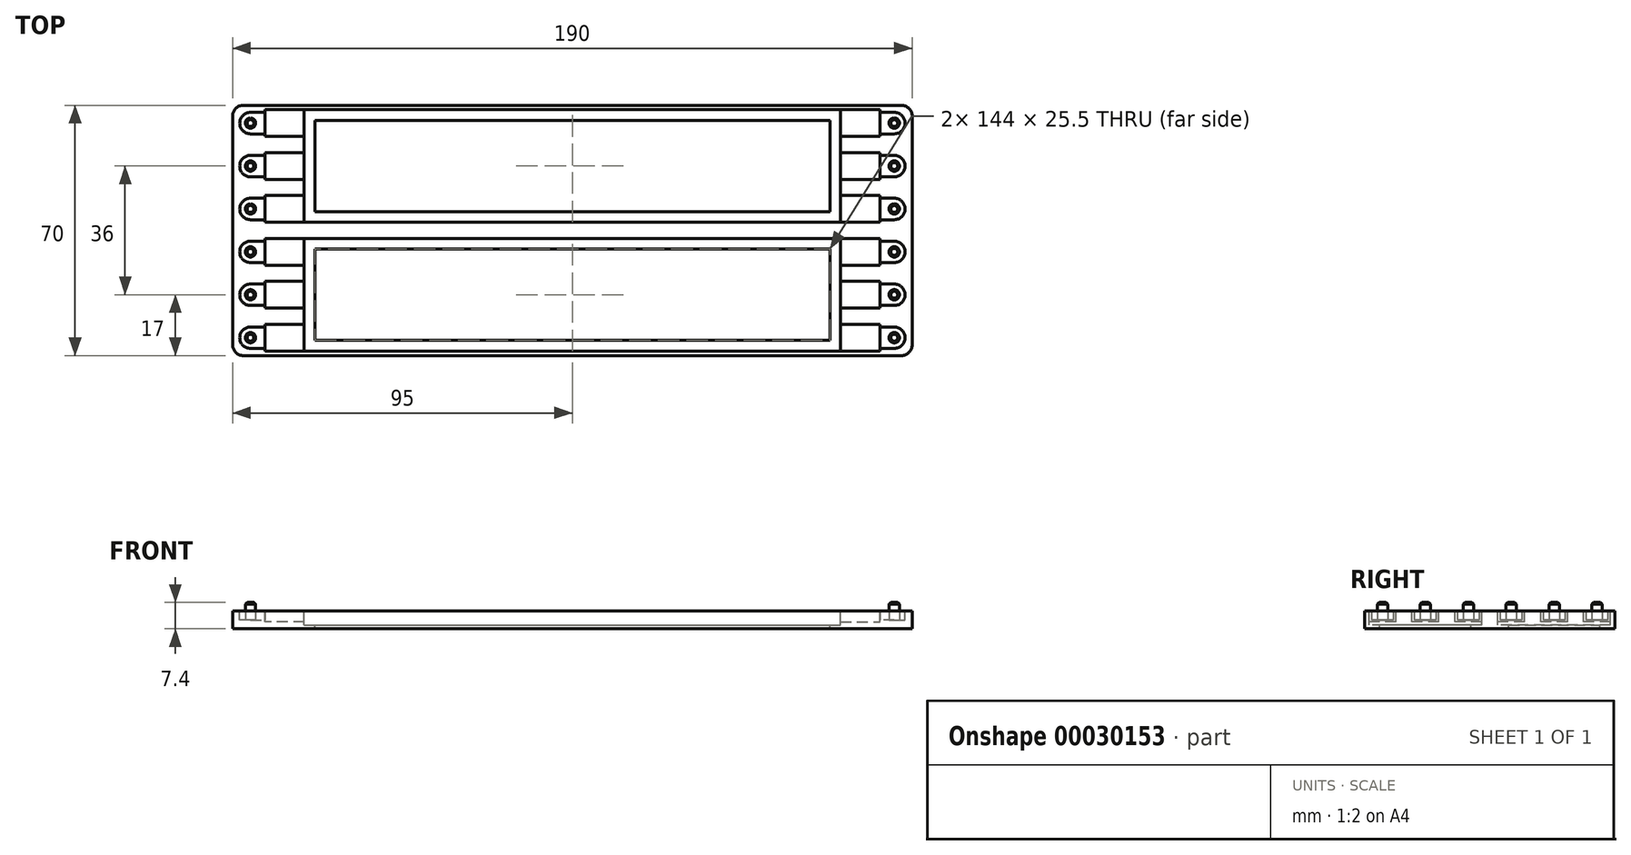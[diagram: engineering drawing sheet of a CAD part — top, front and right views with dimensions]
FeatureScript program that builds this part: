
annotation { "Feature Type Name" : "Feature", "Feature Type Description" : "" }
export const myFeature = defineFeature(function(context is Context, id is Id, definition is map)
    precondition{}
    {
        {
            var Q0;
            Q0=qCreatedBy(makeId("Top.planeOp"),FACE);
            var sketch = newSketch(context, id + "F0", { "sketchPlane" : qUnion([Q0])});
            skLineSegment(sketch, "E0.rect.bottom", {"start": v(-5, 65) * mm, "end": v(15, 65) * mm});
            skLineSegment(sketch, "E0.rect.top", {"start": v(-5, -5) * mm, "end": v(15, -5) * mm});
            skLineSegment(sketch, "E0.rect.left", {"start": v(-5, 65) * mm, "end": v(-5, -5) * mm});
            skLineSegment(sketch, "E0.rect.right", {"start": v(15, 65) * mm, "end": v(15, -5) * mm});
            skCircle(sketch, "E1", {"center": v(0, 0) * mm, "radius": 5 * mm, "construction": true});
            skSolve(sketch);
        }
        {
            var Q0;
            Q0=makeQuery(id+"F0.imprint","IMPRINT",FACE,{"disambiguationData":[TD([[makeQuery(id+"F0.imprint","IMPRINT",EDGE,{"derivedFrom":sQuery(id+"F0.wireOp",EDGE,"E0.rect.bottom")}),-1.0]])]});
            extrude(context, id + "F1", {"entities" : qUnion([Q0]), "depth" : 4 * mm});
        }
        {
            var Q0;
            Q0=makeQuery(id+"F1.opExtrude","CAP_FACE",FACE,{"disambiguationData":[OSD([sQuery(id+"F0.wireOp",EDGE,"E0.rect.bottom"),sQuery(id+"F0.wireOp",EDGE,"E0.rect.top"),sQuery(id+"F0.wireOp",EDGE,"E0.rect.left"),sQuery(id+"F0.wireOp",EDGE,"E0.rect.right")])],"isStart":false});
            var sketch = newSketch(context, id + "F2", { "sketchPlane" : qUnion([Q0])});
            skArc(sketch, "E2", {"start": v(0, 3) * mm, "mid": v(-3, 0) * mm, "end": v(0, -3) * mm});
            skLineSegment(sketch, "E3", {"start": v(0, 3) * mm, "end": v(15, 3) * mm});
            skLineSegment(sketch, "E4", {"start": v(15, 3) * mm, "end": v(15, -3) * mm});
            skLineSegment(sketch, "E5", {"start": v(15, -3) * mm, "end": v(0, -3) * mm});
            skPoint(sketch, "E6", {"position": v(15, 0) * mm});
            skPoint(sketch, "E7.0.1.0", {"position": v(15, 12) * mm});
            skArc(sketch, "E7.0.1.1", {"start": v(0, 15) * mm, "mid": v(-3, 12) * mm, "end": v(0, 9) * mm});
            skLineSegment(sketch, "E7.0.1.2", {"start": v(0, 15) * mm, "end": v(15, 15) * mm});
            skLineSegment(sketch, "E7.0.1.3", {"start": v(15, 15) * mm, "end": v(15, 9) * mm});
            skLineSegment(sketch, "E7.0.1.4", {"start": v(15, 9) * mm, "end": v(0, 9) * mm});
            skPoint(sketch, "E7.0.2.0", {"position": v(15, 24) * mm});
            skArc(sketch, "E7.0.2.1", {"start": v(0, 27) * mm, "mid": v(-3, 24) * mm, "end": v(0, 21) * mm});
            skLineSegment(sketch, "E7.0.2.2", {"start": v(0, 27) * mm, "end": v(15, 27) * mm});
            skLineSegment(sketch, "E7.0.2.3", {"start": v(15, 27) * mm, "end": v(15, 21) * mm});
            skLineSegment(sketch, "E7.0.2.4", {"start": v(15, 21) * mm, "end": v(0, 21) * mm});
            skPoint(sketch, "E7.0.3.0", {"position": v(15, 36) * mm});
            skArc(sketch, "E7.0.3.1", {"start": v(0, 39) * mm, "mid": v(-3, 36) * mm, "end": v(0, 33) * mm});
            skLineSegment(sketch, "E7.0.3.2", {"start": v(0, 39) * mm, "end": v(15, 39) * mm});
            skLineSegment(sketch, "E7.0.3.3", {"start": v(15, 39) * mm, "end": v(15, 33) * mm});
            skLineSegment(sketch, "E7.0.3.4", {"start": v(15, 33) * mm, "end": v(0, 33) * mm});
            skPoint(sketch, "E7.0.4.0", {"position": v(15, 48) * mm});
            skArc(sketch, "E7.0.4.1", {"start": v(0, 51) * mm, "mid": v(-3, 48) * mm, "end": v(0, 45) * mm});
            skLineSegment(sketch, "E7.0.4.2", {"start": v(0, 51) * mm, "end": v(15, 51) * mm});
            skLineSegment(sketch, "E7.0.4.3", {"start": v(15, 51) * mm, "end": v(15, 45) * mm});
            skLineSegment(sketch, "E7.0.4.4", {"start": v(15, 45) * mm, "end": v(0, 45) * mm});
            skPoint(sketch, "E7.0.5.0", {"position": v(15, 60) * mm});
            skArc(sketch, "E7.0.5.1", {"start": v(0, 63) * mm, "mid": v(-3, 60) * mm, "end": v(0, 57) * mm});
            skLineSegment(sketch, "E7.0.5.2", {"start": v(0, 63) * mm, "end": v(15, 63) * mm});
            skLineSegment(sketch, "E7.0.5.3", {"start": v(15, 63) * mm, "end": v(15, 57) * mm});
            skLineSegment(sketch, "E7.0.5.4", {"start": v(15, 57) * mm, "end": v(0, 57) * mm});
            skLineSegment(sketch, "E7.direction1", {"start": v(15, 0) * mm, "end": v(40, 0) * mm, "construction": true});
            skLineSegment(sketch, "E7.direction2", {"start": v(15, 0) * mm, "end": v(15, 12) * mm, "construction": true});
            skLineSegment(sketch, "E8", {"start": v(0, 3) * mm, "end": v(0, -3) * mm, "construction": true});
            skSolve(sketch);
        }
        {
            var Q0;
            Q0 = qSketchRegion(id + "F2", true);
            extrude(context, id + "F3", {"entities" : qUnion([Q0]), "operationType" : NewBodyOperationType.REMOVE, "oppositeDirection" : true, "depth" : 2.6 * mm});
        }
        {
            var Q0;
            Q0=makeQuery(id+"F1.opExtrude","CAP_FACE",FACE,{"disambiguationData":[OSD([sQuery(id+"F0.wireOp",EDGE,"E0.rect.bottom"),sQuery(id+"F0.wireOp",EDGE,"E0.rect.top"),sQuery(id+"F0.wireOp",EDGE,"E0.rect.left"),sQuery(id+"F0.wireOp",EDGE,"E0.rect.right")])],"isStart":false});
            var sketch = newSketch(context, id + "F4", { "sketchPlane" : qUnion([Q0])});
            skLineSegment(sketch, "E9.top", {"start": v(15, 3.75) * mm, "end": v(4, 3.75) * mm});
            skLineSegment(sketch, "E10.top", {"start": v(15, -3.75) * mm, "end": v(4, -3.75) * mm});
            skLineSegment(sketch, "E10.right", {"start": v(4, 3.75) * mm, "end": v(4, -3.75) * mm});
            skCircle(sketch, "E11", {"center": v(0, 0) * mm, "radius": 3 * mm, "construction": true});
            skPoint(sketch, "E11.first.point", {"position": v(-1.02, 2.82) * mm});
            skPoint(sketch, "E11.second.point", {"position": v(-2.95, 0.56) * mm});
            skPoint(sketch, "E11.third.point", {"position": v(-1.82, -2.38) * mm});
            skCircle(sketch, "E12.0.1.0", {"center": v(0, 12) * mm, "radius": 3 * mm, "construction": true});
            skPoint(sketch, "E12.0.1.2", {"position": v(-1.82, 9.62) * mm});
            skPoint(sketch, "E12.0.1.3", {"position": v(-1.02, 14.82) * mm});
            skLineSegment(sketch, "E12.0.1.5", {"start": v(15, 15.75) * mm, "end": v(4, 15.75) * mm});
            skLineSegment(sketch, "E12.0.1.6", {"start": v(15, 8.25) * mm, "end": v(4, 8.25) * mm});
            skPoint(sketch, "E12.0.1.7", {"position": v(-2.95, 12.56) * mm});
            skLineSegment(sketch, "E12.0.1.8", {"start": v(4, 15.75) * mm, "end": v(4, 8.25) * mm});
            skLineSegment(sketch, "E12.0.1.9", {"start": v(4, 15) * mm, "end": v(4, 15.75) * mm});
            skLineSegment(sketch, "E12.0.1.10", {"start": v(15, 15) * mm, "end": v(15, 15.75) * mm});
            skLineSegment(sketch, "E12.0.1.11", {"start": v(15, 9) * mm, "end": v(15, 8.25) * mm});
            skCircle(sketch, "E12.0.2.0", {"center": v(0, 24) * mm, "radius": 3 * mm, "construction": true});
            skPoint(sketch, "E12.0.2.2", {"position": v(-1.82, 21.62) * mm});
            skPoint(sketch, "E12.0.2.3", {"position": v(-1.02, 26.82) * mm});
            skLineSegment(sketch, "E12.0.2.5", {"start": v(15, 27.75) * mm, "end": v(4, 27.75) * mm});
            skLineSegment(sketch, "E12.0.2.6", {"start": v(15, 20.25) * mm, "end": v(4, 20.25) * mm});
            skPoint(sketch, "E12.0.2.7", {"position": v(-2.95, 24.56) * mm});
            skLineSegment(sketch, "E12.0.2.8", {"start": v(4, 27.75) * mm, "end": v(4, 20.25) * mm});
            skLineSegment(sketch, "E12.0.2.9", {"start": v(4, 27) * mm, "end": v(4, 27.75) * mm});
            skLineSegment(sketch, "E12.0.2.10", {"start": v(15, 27) * mm, "end": v(15, 27.75) * mm});
            skLineSegment(sketch, "E12.0.2.11", {"start": v(15, 21) * mm, "end": v(15, 20.25) * mm});
            skCircle(sketch, "E12.0.3.0", {"center": v(0, 36) * mm, "radius": 3 * mm, "construction": true});
            skPoint(sketch, "E12.0.3.2", {"position": v(-1.82, 33.62) * mm});
            skPoint(sketch, "E12.0.3.3", {"position": v(-1.02, 38.82) * mm});
            skLineSegment(sketch, "E12.0.3.5", {"start": v(15, 39.75) * mm, "end": v(4, 39.75) * mm});
            skLineSegment(sketch, "E12.0.3.6", {"start": v(15, 32.25) * mm, "end": v(4, 32.25) * mm});
            skPoint(sketch, "E12.0.3.7", {"position": v(-2.95, 36.56) * mm});
            skLineSegment(sketch, "E12.0.3.8", {"start": v(4, 39.75) * mm, "end": v(4, 32.25) * mm});
            skLineSegment(sketch, "E12.0.3.9", {"start": v(4, 39) * mm, "end": v(4, 39.75) * mm});
            skLineSegment(sketch, "E12.0.3.10", {"start": v(15, 39) * mm, "end": v(15, 39.75) * mm});
            skLineSegment(sketch, "E12.0.3.11", {"start": v(15, 33) * mm, "end": v(15, 32.25) * mm});
            skCircle(sketch, "E12.0.4.0", {"center": v(0, 48) * mm, "radius": 3 * mm, "construction": true});
            skPoint(sketch, "E12.0.4.2", {"position": v(-1.82, 45.62) * mm});
            skPoint(sketch, "E12.0.4.3", {"position": v(-1.02, 50.82) * mm});
            skLineSegment(sketch, "E12.0.4.5", {"start": v(15, 51.75) * mm, "end": v(4, 51.75) * mm});
            skLineSegment(sketch, "E12.0.4.6", {"start": v(15, 44.25) * mm, "end": v(4, 44.25) * mm});
            skPoint(sketch, "E12.0.4.7", {"position": v(-2.95, 48.56) * mm});
            skLineSegment(sketch, "E12.0.4.8", {"start": v(4, 51.75) * mm, "end": v(4, 44.25) * mm});
            skLineSegment(sketch, "E12.0.4.9", {"start": v(4, 51) * mm, "end": v(4, 51.75) * mm});
            skLineSegment(sketch, "E12.0.4.10", {"start": v(15, 51) * mm, "end": v(15, 51.75) * mm});
            skLineSegment(sketch, "E12.0.4.11", {"start": v(15, 45) * mm, "end": v(15, 44.25) * mm});
            skCircle(sketch, "E12.0.5.0", {"center": v(0, 60) * mm, "radius": 3 * mm, "construction": true});
            skPoint(sketch, "E12.0.5.2", {"position": v(-1.82, 57.62) * mm});
            skPoint(sketch, "E12.0.5.3", {"position": v(-1.02, 62.82) * mm});
            skLineSegment(sketch, "E12.0.5.5", {"start": v(15, 63.75) * mm, "end": v(4, 63.75) * mm});
            skLineSegment(sketch, "E12.0.5.6", {"start": v(15, 56.25) * mm, "end": v(4, 56.25) * mm});
            skPoint(sketch, "E12.0.5.7", {"position": v(-2.95, 60.56) * mm});
            skLineSegment(sketch, "E12.0.5.8", {"start": v(4, 63.75) * mm, "end": v(4, 56.25) * mm});
            skLineSegment(sketch, "E12.0.5.9", {"start": v(4, 63) * mm, "end": v(4, 63.75) * mm});
            skLineSegment(sketch, "E12.0.5.10", {"start": v(15, 63) * mm, "end": v(15, 63.75) * mm});
            skLineSegment(sketch, "E12.0.5.11", {"start": v(15, 57) * mm, "end": v(15, 56.25) * mm});
            skLineSegment(sketch, "E12.direction1", {"start": v(0, 0) * mm, "end": v(25, 0) * mm, "construction": true});
            skLineSegment(sketch, "E12.direction2", {"start": v(0, 0) * mm, "end": v(0, 12) * mm, "construction": true});
            skLineSegment(sketch, "E13", {"start": v(15, 3.75) * mm, "end": v(15, -3.75) * mm});
            skPoint(sketch, "E14", {"position": v(15, 0) * mm});
            skLineSegment(sketch, "E15", {"start": v(15, 21) * mm, "end": v(15, 27) * mm});
            skLineSegment(sketch, "E16", {"start": v(15, 33) * mm, "end": v(15, 39) * mm});
            skLineSegment(sketch, "E17", {"start": v(15, 63) * mm, "end": v(15, 57) * mm});
            skLineSegment(sketch, "E18", {"start": v(15, 51) * mm, "end": v(15, 45) * mm});
            skLineSegment(sketch, "E19", {"start": v(15, 15) * mm, "end": v(15, 9) * mm});
            skSolve(sketch);
        }
        {
            var Q0;
            Q0 = qSketchRegion(id + "F4", true);
            var Q1;
            Q1=makeQuery(id+"F3.boolean.opBoolean","COPY",FACE,{"derivedFrom":makeQuery(id+"F3.opExtrude","CAP_FACE",FACE,{"disambiguationData":[OSD([sQuery(id+"F2.wireOp",EDGE,"E2"),sQuery(id+"F2.wireOp",EDGE,"E3"),sQuery(id+"F2.wireOp",EDGE,"E4"),sQuery(id+"F2.wireOp",EDGE,"E5")])],"isStart":false})});
            extrude(context, id + "F5", {"entities" : qUnion([Q0]), "operationType" : NewBodyOperationType.REMOVE, "oppositeDirection" : true, "endBoundEntityFace" : qUnion([Q1]), "depth" : 3 * mm});
        }
        {
            var Q0;
            Q0=makeQuery(id+"F3.boolean.opBoolean","COPY",FACE,{"derivedFrom":makeQuery(id+"F3.opExtrude","CAP_FACE",FACE,{"disambiguationData":[OSD([sQuery(id+"F2.wireOp",EDGE,"E2")])],"isStart":false})});
            var sketch = newSketch(context, id + "F6", { "sketchPlane" : qUnion([Q0])});
            skCircle(sketch, "E20", {"center": v(0, 0) * mm, "radius": 1.45 * mm});
            skCircle(sketch, "E21.0.1.0", {"center": v(0, 12) * mm, "radius": 1.45 * mm});
            skCircle(sketch, "E21.0.2.0", {"center": v(0, 24) * mm, "radius": 1.45 * mm});
            skCircle(sketch, "E21.0.3.0", {"center": v(0, 36) * mm, "radius": 1.45 * mm});
            skCircle(sketch, "E21.0.4.0", {"center": v(0, 48) * mm, "radius": 1.45 * mm});
            skCircle(sketch, "E21.0.5.0", {"center": v(0, 60) * mm, "radius": 1.45 * mm});
            skLineSegment(sketch, "E21.direction1", {"start": v(0, 0) * mm, "end": v(25, 0) * mm, "construction": true});
            skLineSegment(sketch, "E21.direction2", {"start": v(0, 0) * mm, "end": v(0, 12) * mm, "construction": true});
            skSolve(sketch);
        }
        {
            var Q0;
            Q0=makeQuery(id+"F6.imprint","IMPRINT",FACE,{"disambiguationData":[TD([[makeQuery(id+"F6.imprint","IMPRINT",EDGE,{"derivedFrom":sQuery(id+"F6.wireOp",EDGE,"E20")}),1.0]])]});
            var Q1;
            Q1=makeQuery(id+"F6.imprint","IMPRINT",FACE,{"disambiguationData":[TD([[makeQuery(id+"F6.imprint","IMPRINT",EDGE,{"derivedFrom":sQuery(id+"F6.wireOp",EDGE,"E21.0.1.0")}),1.0]])]});
            var Q2;
            Q2=makeQuery(id+"F6.imprint","IMPRINT",FACE,{"disambiguationData":[TD([[makeQuery(id+"F6.imprint","IMPRINT",EDGE,{"derivedFrom":sQuery(id+"F6.wireOp",EDGE,"E21.0.2.0")}),1.0]])]});
            var Q3;
            Q3=makeQuery(id+"F6.imprint","IMPRINT",FACE,{"disambiguationData":[TD([[makeQuery(id+"F6.imprint","IMPRINT",EDGE,{"derivedFrom":sQuery(id+"F6.wireOp",EDGE,"E21.0.3.0")}),1.0]])]});
            var Q4;
            Q4=makeQuery(id+"F6.imprint","IMPRINT",FACE,{"disambiguationData":[TD([[makeQuery(id+"F6.imprint","IMPRINT",EDGE,{"derivedFrom":sQuery(id+"F6.wireOp",EDGE,"E21.0.4.0")}),1.0]])]});
            var Q5;
            Q5=makeQuery(id+"F6.imprint","IMPRINT",FACE,{"disambiguationData":[TD([[makeQuery(id+"F6.imprint","IMPRINT",EDGE,{"derivedFrom":sQuery(id+"F6.wireOp",EDGE,"E21.0.5.0")}),1.0]])]});
            extrude(context, id + "F7", {"entities" : qUnion([Q0, Q1, Q2, Q3, Q4, Q5]), "operationType" : NewBodyOperationType.ADD, "depth" : 5 * mm});
        }
        {
            var Q0;
            Q0=makeQuery(id+"F7.opExtrude","CAP_EDGE",EDGE,{"disambiguationData":[OSD([sQuery(id+"F6.wireOp",EDGE,"E20")])],"isStart":false});
            var Q1;
            Q1=makeQuery(id+"F7.opExtrude","CAP_EDGE",EDGE,{"disambiguationData":[OSD([sQuery(id+"F6.wireOp",EDGE,"E21.0.1.0")])],"isStart":false});
            var Q2;
            Q2=makeQuery(id+"F7.opExtrude","CAP_EDGE",EDGE,{"disambiguationData":[OSD([sQuery(id+"F6.wireOp",EDGE,"E21.0.2.0")])],"isStart":false});
            var Q3;
            Q3=makeQuery(id+"F7.opExtrude","CAP_EDGE",EDGE,{"disambiguationData":[OSD([sQuery(id+"F6.wireOp",EDGE,"E21.0.3.0")])],"isStart":false});
            var Q4;
            Q4=makeQuery(id+"F7.opExtrude","CAP_EDGE",EDGE,{"disambiguationData":[OSD([sQuery(id+"F6.wireOp",EDGE,"E21.0.5.0")])],"isStart":false});
            var Q5;
            Q5=makeQuery(id+"F7.opExtrude","CAP_EDGE",EDGE,{"disambiguationData":[OSD([sQuery(id+"F6.wireOp",EDGE,"E21.0.4.0")])],"isStart":false});
            chamfer(context, id + "F8", {"entities" : qUnion([Q0, Q1, Q2, Q3, Q4, Q5]), "width" : .5 * mm, "tangentPropagation" : true});
        }
        {
            var Q0;
            Q0=makeQuery(id+"F1.opExtrude","CAP_FACE",FACE,{"disambiguationData":[OSD([sQuery(id+"F0.wireOp",EDGE,"E0.rect.bottom"),sQuery(id+"F0.wireOp",EDGE,"E0.rect.top"),sQuery(id+"F0.wireOp",EDGE,"E0.rect.left"),sQuery(id+"F0.wireOp",EDGE,"E0.rect.right")])],"isStart":true});
            var sketch = newSketch(context, id + "F9", { "sketchPlane" : qUnion([Q0])});
            skSolve(sketch);
        }
        {
            var Q0;
            Q0=makeQuery(id+"F9.imprint","IMPRINT",FACE,{"disambiguationData":[TD([[makeQuery(id+"F9.imprint","IMPRINT",EDGE,{"derivedFrom":makeQuery(id+"F1.opExtrude","CAP_EDGE",EDGE,{"disambiguationData":[OSD([sQuery(id+"F0.wireOp",EDGE,"E0.rect.bottom")])],"isStart":true})}),1.0]])]});
            var sketch = newSketch(context, id + "F10", { "sketchPlane" : qUnion([Q0])});
            skLineSegment(sketch, "E22.bottom", {"start": v(-5, 5) * mm, "end": v(90, 5) * mm});
            skLineSegment(sketch, "E22.top", {"start": v(-5, -65) * mm, "end": v(90, -65) * mm});
            skLineSegment(sketch, "E22.left", {"start": v(-5, 5) * mm, "end": v(-5, -65) * mm});
            skLineSegment(sketch, "E22.right", {"start": v(90, 5) * mm, "end": v(90, -65) * mm});
            skSolve(sketch);
        }
        {
            var Q0;
            {var subQ2=sQuery(id+"F10.wireOp",EDGE,"E22.right");Q0=makeQuery(id+"F10.imprint","IMPRINT",FACE,{"disambiguationData":[TD([[makeQuery(id+"F10.imprint","IMPRINT",EDGE,{"derivedFrom":subQ2}),-1.0]])]});}
            var Q1;
            Q1=makeQuery(id+"F9.imprint","IMPRINT",FACE,{"disambiguationData":[TD([[makeQuery(id+"F9.imprint","IMPRINT",EDGE,{"derivedFrom":makeQuery(id+"F1.opExtrude","CAP_EDGE",EDGE,{"disambiguationData":[OSD([sQuery(id+"F0.wireOp",EDGE,"E0.rect.bottom")])],"isStart":true})}),1.0]])]});
            extrude(context, id + "F11", {"entities" : qUnion([Q0, Q1]), "operationType" : NewBodyOperationType.ADD, "depth" : 1 * mm});
        }
        {
            var Q0;
            Q0=makeQuery(id+"F11.opExtrude","SWEPT_FACE",FACE,{"disambiguationData":[OSD([sQuery(id+"F10.wireOp",EDGE,"E22.right")])]});
            cPlane(context, id + "F12", {"entities" : qUnion([Q0]), "cplaneType" : CPlaneType.OFFSET, "offset" : 0 * mm, "width" : 150 * mm, "height" : 150 * mm});
        }
        {
            var Q0;
            Q0=makeQuery(id+"F1.opExtrude","SWEPT_BODY",BODY,{"disambiguationData":[OSD([sQuery(id+"F0.wireOp",EDGE,"E0.rect.bottom"),sQuery(id+"F0.wireOp",EDGE,"E0.rect.top"),sQuery(id+"F0.wireOp",EDGE,"E0.rect.left"),sQuery(id+"F0.wireOp",EDGE,"E0.rect.right")])]});
            var Q1;
            Q1=qCreatedBy(id+"F12.planeOp",FACE);
            mirror(context, id + "F13", {"operationType" : NewBodyOperationType.ADD, "entities" : qUnion([Q0]), "mirrorPlane" : qUnion([Q1])});
        }
        {
            var Q0;
            Q0=makeQuery(id+"F1.opExtrude","CAP_FACE",FACE,{"disambiguationData":[OSD([sQuery(id+"F0.wireOp",EDGE,"E0.rect.bottom"),sQuery(id+"F0.wireOp",EDGE,"E0.rect.top"),sQuery(id+"F0.wireOp",EDGE,"E0.rect.left"),sQuery(id+"F0.wireOp",EDGE,"E0.rect.right")])],"isStart":false});
            var sketch = newSketch(context, id + "F14", { "sketchPlane" : qUnion([Q0])});
            skLineSegment(sketch, "E23.bottom", {"start": v(15, -5) * mm, "end": v(165, -5) * mm});
            skLineSegment(sketch, "E23.top", {"start": v(15, -3.75) * mm, "end": v(165, -3.75) * mm});
            skLineSegment(sketch, "E23.left", {"start": v(15, -5) * mm, "end": v(15, -3.75) * mm});
            skLineSegment(sketch, "E23.right", {"start": v(165, -5) * mm, "end": v(165, -3.75) * mm});
            skLineSegment(sketch, "E24.bottom", {"start": v(15, 27.75) * mm, "end": v(165, 27.75) * mm});
            skLineSegment(sketch, "E24.top", {"start": v(15, 32.25) * mm, "end": v(165, 32.25) * mm});
            skLineSegment(sketch, "E24.left", {"start": v(15, 27.75) * mm, "end": v(15, 32.25) * mm});
            skLineSegment(sketch, "E24.right", {"start": v(165, 27.75) * mm, "end": v(165, 32.25) * mm});
            skLineSegment(sketch, "E25.bottom", {"start": v(15, 65) * mm, "end": v(165, 65) * mm});
            skLineSegment(sketch, "E25.top", {"start": v(15, 63.75) * mm, "end": v(165, 63.75) * mm});
            skLineSegment(sketch, "E25.left", {"start": v(15, 65) * mm, "end": v(15, 63.75) * mm});
            skLineSegment(sketch, "E25.right", {"start": v(165, 65) * mm, "end": v(165, 63.75) * mm});
            skSolve(sketch);
        }
        {
            var Q0;
            Q0 = qSketchRegion(id + "F14", true);
            extrude(context, id + "F15", {"entities" : qUnion([Q0]), "operationType" : NewBodyOperationType.ADD, "endBound" : BoundingType.UP_TO_NEXT, "oppositeDirection" : true, "depth" : 25 * mm});
        }
        {
            var Q0;
            {var subQ0=makeQuery(id+"F5.boolean.opBoolean","COPY",FACE,{"derivedFrom":makeQuery(id+"F5.opExtrude","SWEPT_FACE",FACE,{"disambiguationData":[OSD([sQuery(id+"F4.wireOp",EDGE,"E10.top")])]})});var subQ2=sQuery(id+"F0.wireOp",EDGE,"E0.rect.right");var subQ4=makeQuery(id+"F11.boolean.opBoolean","MERGE",FACE,{"derivedFrom":[makeQuery(id+"F11.opExtrude","CAP_FACE",FACE,{"disambiguationData":[OSD([sQuery(id+"F0.wireOp",EDGE,"E0.rect.bottom"),sQuery(id+"F0.wireOp",EDGE,"E0.rect.top"),sQuery(id+"F0.wireOp",EDGE,"E0.rect.left"),subQ2])],"isStart":true}),makeQuery(id+"F11.opExtrude","CAP_FACE",FACE,{"disambiguationData":[OSD([subQ2,sQuery(id+"F10.wireOp",EDGE,"E22.bottom"),sQuery(id+"F10.wireOp",EDGE,"E22.top"),sQuery(id+"F10.wireOp",EDGE,"E22.right")])],"isStart":true})]});Q0=makeQuery(id+"F15.boolean.opBoolean","SPLIT",FACE,{"disambiguationData":[TD([subQ0])],"derivedFrom":makeQuery(id+"F13.boolean.opBoolean","MERGE",FACE,{"derivedFrom":[subQ4,makeQuery(id+"F13.opPattern","COPY",FACE,{"derivedFrom":subQ4,"instanceName":"1"})]})});}
            var sketch = newSketch(context, id + "F16", { "sketchPlane" : qUnion([Q0])});
            skLineSegment(sketch, "E26.bottom", {"start": v(15, 27.75) * mm, "end": v(165, 27.75) * mm, "construction": true});
            skLineSegment(sketch, "E26.top", {"start": v(15, -3.75) * mm, "end": v(165, -3.75) * mm, "construction": true});
            skLineSegment(sketch, "E26.left", {"start": v(15, 27.75) * mm, "end": v(15, -3.75) * mm, "construction": true});
            skLineSegment(sketch, "E26.right", {"start": v(165, 27.75) * mm, "end": v(165, -3.75) * mm, "construction": true});
            skLineSegment(sketch, "E27.0", {"start": v(18, -0.75) * mm, "end": v(162, -0.75) * mm});
            skLineSegment(sketch, "E27.1", {"start": v(18, 24.75) * mm, "end": v(18, -0.75) * mm});
            skLineSegment(sketch, "E27.2", {"start": v(18, 24.75) * mm, "end": v(162, 24.75) * mm});
            skLineSegment(sketch, "E27.3", {"start": v(162, 24.75) * mm, "end": v(162, -0.75) * mm});
            skLineSegment(sketch, "E28", {"start": v(15, 27.75) * mm, "end": v(15, 32.25) * mm, "construction": true});
            skPoint(sketch, "E29", {"position": v(15, 30) * mm});
            skLineSegment(sketch, "E30", {"start": v(165, 27.75) * mm, "end": v(165, 32.25) * mm, "construction": true});
            skPoint(sketch, "E31", {"position": v(165, 30) * mm});
            skLineSegment(sketch, "E32", {"start": v(165, 30) * mm, "end": v(15, 30) * mm, "construction": true});
            skLineSegment(sketch, "E33.MirrorCS", {"start": v(18, 35.25) * mm, "end": v(18, 60.75) * mm});
            skLineSegment(sketch, "E34.MirrorCS", {"start": v(18, 60.75) * mm, "end": v(162, 60.75) * mm});
            skLineSegment(sketch, "E35.MirrorCS", {"start": v(162, 35.25) * mm, "end": v(162, 60.75) * mm});
            skLineSegment(sketch, "E36.MirrorCS", {"start": v(18, 35.25) * mm, "end": v(162, 35.25) * mm});
            skSolve(sketch);
        }
        {
            var Q0;
            Q0 = qSketchRegion(id + "F16", true);
            extrude(context, id + "F17", {"entities" : qUnion([Q0]), "operationType" : NewBodyOperationType.REMOVE, "endBound" : BoundingType.UP_TO_NEXT, "oppositeDirection" : true, "depth" : 25 * mm});
        }
        {
            var Q0;
            {var subQ0=sQuery(id+"F0.wireOp",EDGE,"E0.rect.top");var subQ1=sQuery(id+"F0.wireOp",EDGE,"E0.rect.left");Q0=makeQuery(id+"F11.boolean.opBoolean","MERGE",EDGE,{"derivedFrom":[makeQuery(id+"F1.opExtrude","SWEPT_EDGE",EDGE,{"disambiguationData":[OSD([subQ0,subQ1])]}),makeQuery(id+"F11.opExtrude","SWEPT_EDGE",EDGE,{"disambiguationData":[OSD([subQ0,subQ1])]})]});}
            var Q1;
            {var subQ0=sQuery(id+"F0.wireOp",EDGE,"E0.rect.top");var subQ1=sQuery(id+"F0.wireOp",EDGE,"E0.rect.left");Q1=makeQuery(id+"F13.opPattern","COPY",EDGE,{"derivedFrom":makeQuery(id+"F11.boolean.opBoolean","MERGE",EDGE,{"derivedFrom":[makeQuery(id+"F1.opExtrude","SWEPT_EDGE",EDGE,{"disambiguationData":[OSD([subQ0,subQ1])]}),makeQuery(id+"F11.opExtrude","SWEPT_EDGE",EDGE,{"disambiguationData":[OSD([subQ0,subQ1])]})]}),"instanceName":"1"});}
            var Q2;
            {var subQ0=sQuery(id+"F0.wireOp",EDGE,"E0.rect.bottom");var subQ1=sQuery(id+"F0.wireOp",EDGE,"E0.rect.left");Q2=makeQuery(id+"F13.opPattern","COPY",EDGE,{"derivedFrom":makeQuery(id+"F11.boolean.opBoolean","MERGE",EDGE,{"derivedFrom":[makeQuery(id+"F1.opExtrude","SWEPT_EDGE",EDGE,{"disambiguationData":[OSD([subQ0,subQ1])]}),makeQuery(id+"F11.opExtrude","SWEPT_EDGE",EDGE,{"disambiguationData":[OSD([subQ0,subQ1])]})]}),"instanceName":"1"});}
            var Q3;
            {var subQ0=sQuery(id+"F0.wireOp",EDGE,"E0.rect.bottom");var subQ1=sQuery(id+"F0.wireOp",EDGE,"E0.rect.left");Q3=makeQuery(id+"F11.boolean.opBoolean","MERGE",EDGE,{"derivedFrom":[makeQuery(id+"F1.opExtrude","SWEPT_EDGE",EDGE,{"disambiguationData":[OSD([subQ0,subQ1])]}),makeQuery(id+"F11.opExtrude","SWEPT_EDGE",EDGE,{"disambiguationData":[OSD([subQ0,subQ1])]})]});}
            fillet(context, id + "F18", {"entities" : qUnion([Q0, Q1, Q2, Q3]), "radius" : 3 * mm, "tangentPropagation" : true, "allowEdgeOverflow" : false});
        }
    });
